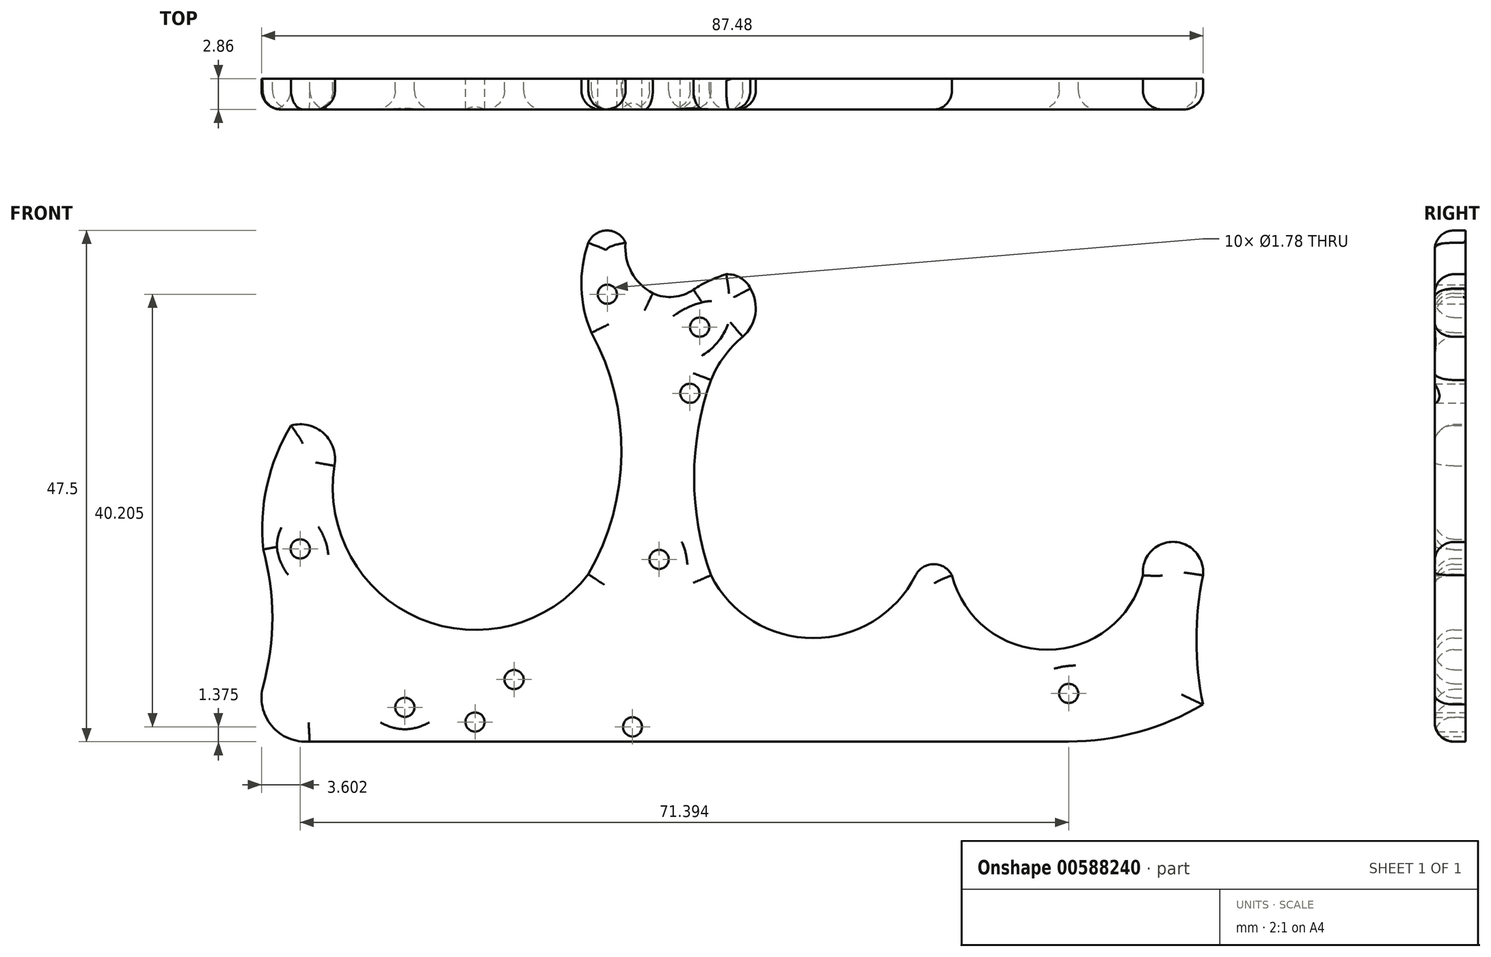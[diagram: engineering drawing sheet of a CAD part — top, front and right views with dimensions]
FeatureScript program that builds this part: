
annotation { "Feature Type Name" : "Feature", "Feature Type Description" : "" }
export const myFeature = defineFeature(function(context is Context, id is Id, definition is map)
    precondition{}
    {
        {
            var Q0;
            Q0=qCreatedBy(makeId("Front.planeOp"),FACE);
            var sketch = newSketch(context, id + "F0", { "sketchPlane" : qUnion([Q0])});
            skArc(sketch, "E0", {"start": v(-15.69, 7.63) * mm, "mid": v(-12.62, 18.81) * mm, "end": v(-15.4, 30.08) * mm});
            skArc(sketch, "E1", {"start": v(-39.29, 17.7) * mm, "mid": v(-31.4, 3.51) * mm, "end": v(-15.69, 7.63) * mm});
            skArc(sketch, "E2", {"start": v(41.4, 7.53) * mm, "mid": v(38.62, 10.63) * mm, "end": v(35.84, 7.53) * mm});
            skArc(sketch, "E3", {"start": v(-4.3, 25.68) * mm, "mid": v(-5.87, 16.6) * mm, "end": v(-4.3, 7.53) * mm});
            skArc(sketch, "E4", {"start": v(-15.69, 38.42) * mm, "mid": v(-16.34, 34.22) * mm, "end": v(-15.4, 30.08) * mm});
            skLineSegment(sketch, "E5", {"start": v(-7.91, -7.91) * mm, "end": v(28.92, -7.91) * mm});
            skArc(sketch, "E6", {"start": v(-43.31, 21.44) * mm, "mid": v(-45.54, 15.9) * mm, "end": v(-45.9, 9.93) * mm});
            skArc(sketch, "E7", {"start": v(-45.9, -2.73) * mm, "mid": v(-45.03, 3.6) * mm, "end": v(-45.9, 9.93) * mm});
            skLineSegment(sketch, "E8", {"start": v(-7.91, -7.91) * mm, "end": v(-41.59, -7.91) * mm});
            skArc(sketch, "E9", {"start": v(-45.9, -2.73) * mm, "mid": v(-45.1, -6.46) * mm, "end": v(-41.59, -7.91) * mm});
            skArc(sketch, "E10", {"start": v(41.4, 7.53) * mm, "mid": v(40.8, 1.52) * mm, "end": v(41.4, -4.48) * mm});
            skArc(sketch, "E11", {"start": v(28.92, -7.91) * mm, "mid": v(35.4, -7.04) * mm, "end": v(41.4, -4.48) * mm});
            skArc(sketch, "E12", {"start": v(-4.3, 7.53) * mm, "mid": v(5.2, 1.69) * mm, "end": v(14.7, 7.53) * mm});
            skArc(sketch, "E13", {"start": v(18.09, 7.53) * mm, "mid": v(26.96, 0.6) * mm, "end": v(35.84, 7.53) * mm});
            skArc(sketch, "E14", {"start": v(14.7, 7.53) * mm, "mid": v(16.4, 8.57) * mm, "end": v(18.09, 7.53) * mm});
            skPoint(sketch, "E15", {"position": v(-22.6, -2.16) * mm});
            skArc(sketch, "E16", {"start": v(-39.29, 17.7) * mm, "mid": v(-40.25, 20.7) * mm, "end": v(-43.31, 21.44) * mm});
            skArc(sketch, "E17", {"start": v(-1.35, 29.7) * mm, "mid": v(-3.07, 27.87) * mm, "end": v(-4.3, 25.68) * mm});
            skArc(sketch, "E18", {"start": v(-1.35, 29.7) * mm, "mid": v(-0.18, 31.8) * mm, "end": v(-0.64, 34.17) * mm});
            skArc(sketch, "E19", {"start": v(-0.64, 34.17) * mm, "mid": v(-1.55, 35.18) * mm, "end": v(-2.88, 35.5) * mm});
            skArc(sketch, "E20", {"start": v(-2.88, 35.5) * mm, "mid": v(-4.46, 34.9) * mm, "end": v(-5.93, 34.07) * mm});
            skArc(sketch, "E21", {"start": v(-9.7, 33.73) * mm, "mid": v(-7.77, 33.4) * mm, "end": v(-5.93, 34.07) * mm});
            skArc(sketch, "E22", {"start": v(-12.23, 38.42) * mm, "mid": v(-11.68, 35.69) * mm, "end": v(-9.7, 33.73) * mm});
            skArc(sketch, "E23", {"start": v(-12.23, 38.42) * mm, "mid": v(-13.96, 39.57) * mm, "end": v(-15.69, 38.42) * mm});
            skPoint(sketch, "E24", {"position": v(-5.35, 30.58) * mm});
            skPoint(sketch, "E25", {"position": v(-9.12, 9) * mm});
            skPoint(sketch, "E26", {"position": v(-32.74, -4.74) * mm});
            skPoint(sketch, "E27", {"position": v(-42.46, 9.98) * mm});
            skPoint(sketch, "E28", {"position": v(28.94, -3.45) * mm});
            skPoint(sketch, "E29", {"position": v(-13.92, 33.65) * mm});
            skPoint(sketch, "E30", {"position": v(-26.22, -6.1) * mm});
            skPoint(sketch, "E31", {"position": v(-11.59, -6.55) * mm});
            skPoint(sketch, "E32", {"position": v(-6.26, 24.44) * mm});
            skSolve(sketch);
        }
        {
            var Q0;
            Q0=makeQuery(id+"F0.imprint","IMPRINT",FACE,{"disambiguationData":[TD([[makeQuery(id+"F0.imprint","IMPRINT",EDGE,{"derivedFrom":sQuery(id+"F0.wireOp",EDGE,"E0")}),-1.0]])]});
            extrude(context, id + "F1", {"entities" : qUnion([Q0]), "depth" : 2.86 * mm, "offsetDistance" : 25.4 * mm});
        }
        {
            var Q0;
            Q0=sQuery(id+"F0.wireOp",VERTEX,"4d9ed20c-a050-41b1-a726-ba9a68d03454");
            var Q1;
            Q1=sQuery(id+"F0.wireOp",VERTEX,"f05e3413-97fa-4317-9460-9a704415e28e");
            var Q2;
            Q2=sQuery(id+"F0.wireOp",VERTEX,"E15");
            var Q3;
            Q3=sQuery(id+"F0.wireOp",VERTEX,"ca89f7f3-d3c6-4f0c-a5c2-640b6aec9d28");
            var Q4;
            Q4=sQuery(id+"F0.wireOp",VERTEX,"cdc7b90f-4f78-4515-b2b2-9dd8b976f43d");
            var Q5;
            Q5=sQuery(id+"F0.wireOp",VERTEX,"E24");
            var Q6;
            Q6=sQuery(id+"F0.wireOp",VERTEX,"0d2d3b97-50c2-489a-9959-e3951f0aeffd");
            var Q7;
            Q7=sQuery(id+"F0.wireOp",VERTEX,"E25");
            var Q8;
            Q8=sQuery(id+"F0.wireOp",VERTEX,"9ed7a9c9-4632-4ed3-ae27-16036feed5c8");
            var Q9;
            Q9=sQuery(id+"F0.wireOp",VERTEX,"9a4e39e4-95d2-4212-8172-b782fcab2ba0");
            var Q10;
            Q10=sQuery(id+"F0.wireOp",VERTEX,"E26");
            var Q11;
            Q11=sQuery(id+"F0.wireOp",VERTEX,"E27");
            var Q12;
            Q12=sQuery(id+"F0.wireOp",VERTEX,"E28");
            var Q13;
            Q13=makeQuery(id+"F1.opExtrude","SWEPT_BODY",BODY,{"disambiguationData":[OSD([sQuery(id+"F0.wireOp",EDGE,"E0"),sQuery(id+"F0.wireOp",EDGE,"E1"),sQuery(id+"F0.wireOp",EDGE,"E2"),sQuery(id+"F0.wireOp",EDGE,"E3"),sQuery(id+"F0.wireOp",EDGE,"3EEqmpVa-sYtS-nlyx-7368-GrBW48sy61ME"),sQuery(id+"F0.wireOp",EDGE,"UqaOKMos-FZ6l-7GI9-J2aR-ZYlEZ6ikFnGb"),sQuery(id+"F0.wireOp",EDGE,"SGjXxW1m-KlGl-boIV-9Onv-vCJ5jf5MEAHU"),sQuery(id+"F0.wireOp",EDGE,"487ae1e9-430a-4b7e-8a56-f4b97fb80ecd"),sQuery(id+"F0.wireOp",EDGE,"E4"),sQuery(id+"F0.wireOp",EDGE,"E5"),sQuery(id+"F0.wireOp",EDGE,"E6"),sQuery(id+"F0.wireOp",EDGE,"E7"),sQuery(id+"F0.wireOp",EDGE,"E8"),sQuery(id+"F0.wireOp",EDGE,"E9"),sQuery(id+"F0.wireOp",EDGE,"E10"),sQuery(id+"F0.wireOp",EDGE,"E11"),sQuery(id+"F0.wireOp",EDGE,"E12"),sQuery(id+"F0.wireOp",EDGE,"E13"),sQuery(id+"F0.wireOp",EDGE,"E14"),sQuery(id+"F0.wireOp",EDGE,"E16")])]});
            hole(context, id + "F2", {"style" : HoleStyle.SIMPLE, "endStyle" : HoleEndStyle.THROUGH, "oppositeDirection" : true, "holeDiameter" : 1.78 * mm, "majorDiameter" : 2.18 * mm, "isTappedThrough" : true, "tappedDepth" : 12.7 * mm, "tapClearance" : 3, "locations" : qUnion([Q0, Q1, Q2, Q3, Q4, Q5, Q6, Q7, Q8, Q9, Q10, Q11, Q12]), "scope" : qUnion([Q13])});
        }
        {
            var Q0;
            Q0=makeQuery(id+"F1.opExtrude","CAP_FACE",FACE,{"disambiguationData":[OSD([sQuery(id+"F0.wireOp",EDGE,"E0"),sQuery(id+"F0.wireOp",EDGE,"E1"),sQuery(id+"F0.wireOp",EDGE,"E2"),sQuery(id+"F0.wireOp",EDGE,"E3"),sQuery(id+"F0.wireOp",EDGE,"E4"),sQuery(id+"F0.wireOp",EDGE,"E5"),sQuery(id+"F0.wireOp",EDGE,"E6"),sQuery(id+"F0.wireOp",EDGE,"E7"),sQuery(id+"F0.wireOp",EDGE,"E8"),sQuery(id+"F0.wireOp",EDGE,"E9"),sQuery(id+"F0.wireOp",EDGE,"E10"),sQuery(id+"F0.wireOp",EDGE,"E11"),sQuery(id+"F0.wireOp",EDGE,"E12"),sQuery(id+"F0.wireOp",EDGE,"E13"),sQuery(id+"F0.wireOp",EDGE,"E14"),sQuery(id+"F0.wireOp",EDGE,"E16"),sQuery(id+"F0.wireOp",EDGE,"E17"),sQuery(id+"F0.wireOp",EDGE,"E18"),sQuery(id+"F0.wireOp",EDGE,"E19"),sQuery(id+"F0.wireOp",EDGE,"E20"),sQuery(id+"F0.wireOp",EDGE,"E21"),sQuery(id+"F0.wireOp",EDGE,"E22"),sQuery(id+"F0.wireOp",EDGE,"E23")])],"isStart":false});
            fillet(context, id + "F3", {"entities" : qUnion([Q0]), "radius" : 1.78 * mm, "tangentPropagation" : true, "allowEdgeOverflow" : false});
        }
        {
            var Q0;
            Q0=makeQuery(id+"F1.opExtrude","CAP_EDGE",EDGE,{"disambiguationData":[OSD([sQuery(id+"F0.wireOp",EDGE,"E22")])],"isStart":true});
            var Q1;
            Q1=makeQuery(id+"F1.opExtrude","CAP_EDGE",EDGE,{"disambiguationData":[OSD([sQuery(id+"F0.wireOp",EDGE,"E21")])],"isStart":true});
            var Q2;
            Q2=makeQuery(id+"F1.opExtrude","CAP_EDGE",EDGE,{"disambiguationData":[OSD([sQuery(id+"F0.wireOp",EDGE,"E20")])],"isStart":true});
            fillet(context, id + "F4", {"entities" : qUnion([Q0, Q1, Q2]), "radius" : 0.25 * mm, "tangentPropagation" : true, "allowEdgeOverflow" : false});
        }
        {
            var Q0;
            Q0=sQuery(id+"F0.wireOp",VERTEX,"E29");
            var Q1;
            Q1=sQuery(id+"F0.wireOp",VERTEX,"E30");
            var Q2;
            Q2=sQuery(id+"F0.wireOp",VERTEX,"E31");
            var Q3;
            Q3=sQuery(id+"F0.wireOp",VERTEX,"E32");
            var Q4;
            Q4=makeQuery(id+"F1.opExtrude","SWEPT_BODY",BODY,{"disambiguationData":[OSD([sQuery(id+"F0.wireOp",EDGE,"E0"),sQuery(id+"F0.wireOp",EDGE,"E1"),sQuery(id+"F0.wireOp",EDGE,"E2"),sQuery(id+"F0.wireOp",EDGE,"E3"),sQuery(id+"F0.wireOp",EDGE,"E4"),sQuery(id+"F0.wireOp",EDGE,"E5"),sQuery(id+"F0.wireOp",EDGE,"E6"),sQuery(id+"F0.wireOp",EDGE,"E7"),sQuery(id+"F0.wireOp",EDGE,"E8"),sQuery(id+"F0.wireOp",EDGE,"E9"),sQuery(id+"F0.wireOp",EDGE,"E10"),sQuery(id+"F0.wireOp",EDGE,"E11"),sQuery(id+"F0.wireOp",EDGE,"E12"),sQuery(id+"F0.wireOp",EDGE,"E13"),sQuery(id+"F0.wireOp",EDGE,"E14"),sQuery(id+"F0.wireOp",EDGE,"E16"),sQuery(id+"F0.wireOp",EDGE,"E17"),sQuery(id+"F0.wireOp",EDGE,"E18"),sQuery(id+"F0.wireOp",EDGE,"E19"),sQuery(id+"F0.wireOp",EDGE,"E20"),sQuery(id+"F0.wireOp",EDGE,"E21"),sQuery(id+"F0.wireOp",EDGE,"E22"),sQuery(id+"F0.wireOp",EDGE,"E23")])]});
            hole(context, id + "F5", {"style" : HoleStyle.SIMPLE, "endStyle" : HoleEndStyle.THROUGH, "oppositeDirection" : true, "holeDiameter" : 1.78 * mm, "majorDiameter" : 6.35 * mm, "isTappedThrough" : true, "tappedDepth" : 12.7 * mm, "tapClearance" : 3, "locations" : qUnion([Q0, Q1, Q2, Q3]), "scope" : qUnion([Q4])});
        }
    });
